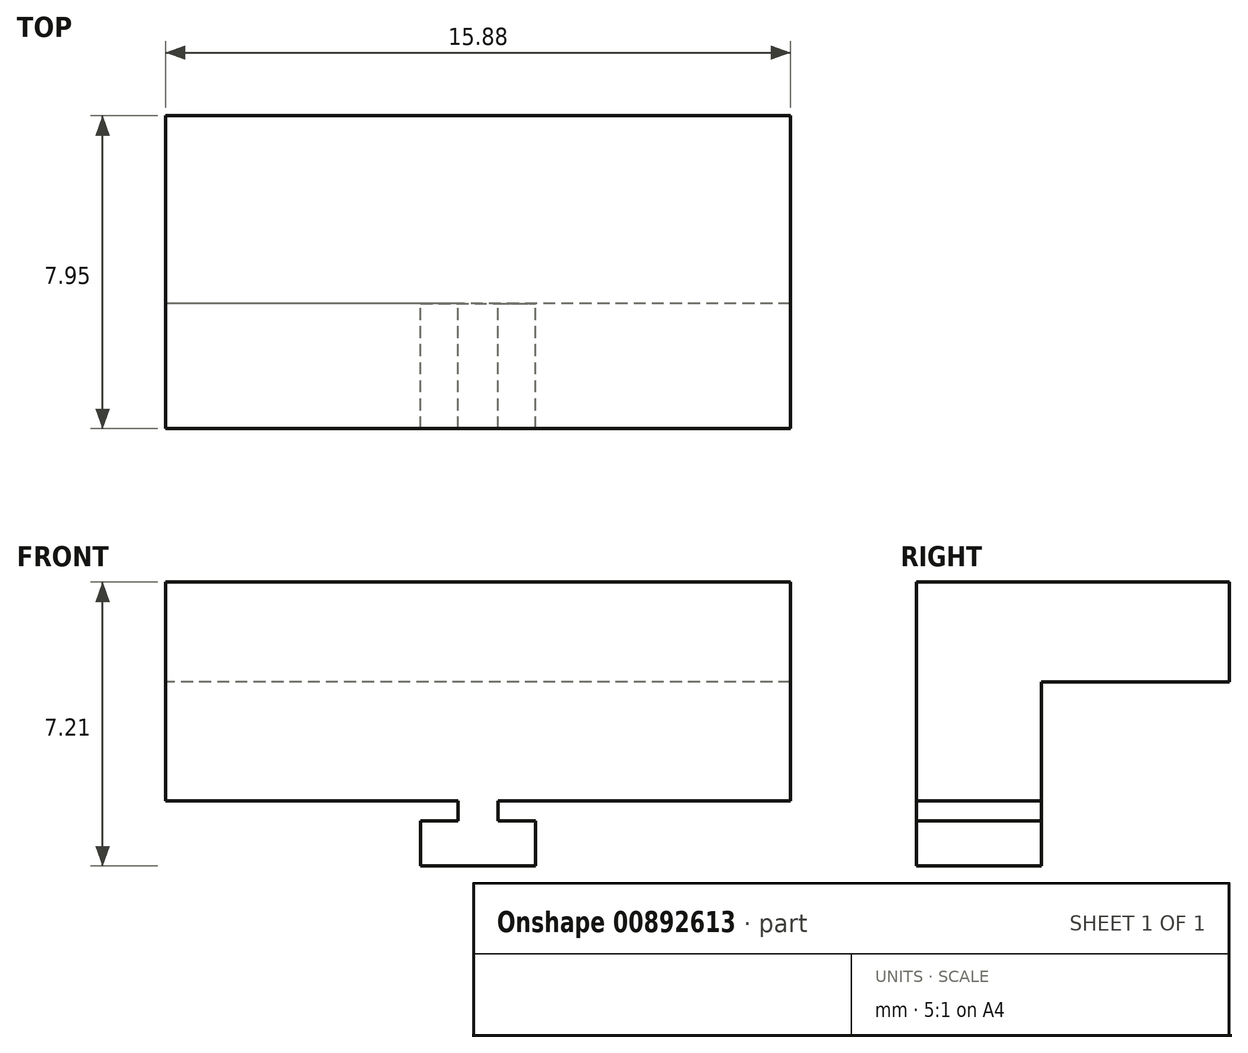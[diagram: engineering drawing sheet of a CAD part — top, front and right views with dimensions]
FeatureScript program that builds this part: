
annotation { "Feature Type Name" : "Feature", "Feature Type Description" : "" }
export const myFeature = defineFeature(function(context is Context, id is Id, definition is map)
    precondition{}
    {
        {
            var Q0;
            Q0=qCreatedBy(makeId("Top.planeOp"),FACE);
            var sketch = newSketch(context, id + "F0", { "sketchPlane" : qUnion([Q0])});
            skLineSegment(sketch, "E0.bottom", {"start": v(7.94, -1.59) * mm, "end": v(-7.94, -1.59) * mm});
            skLineSegment(sketch, "E0.top", {"start": v(7.94, 1.59) * mm, "end": v(-7.94, 1.59) * mm});
            skLineSegment(sketch, "E0.left", {"start": v(7.94, -1.59) * mm, "end": v(7.94, 1.59) * mm});
            skLineSegment(sketch, "E0.right", {"start": v(-7.94, -1.59) * mm, "end": v(-7.94, 1.59) * mm});
            skPoint(sketch, "E0.middle", {"position": v(0, 0) * mm});
            skSolve(sketch);
        }
        {
            var Q0;
            Q0=makeQuery(id+"F0.imprint","IMPRINT",FACE,{"disambiguationData":[TD([[makeQuery(id+"F0.imprint","IMPRINT",EDGE,{"derivedFrom":sQuery(id+"F0.wireOp",EDGE,"E0.bottom")}),-1.0]])]});
            extrude(context, id + "F1", {"entities" : qUnion([Q0]), "depth" : 5.56 * mm, "offsetDistance" : 25.4 * mm});
        }
        {
            var Q0;
            Q0=makeQuery(id+"F1.opExtrude","SWEPT_FACE",FACE,{"disambiguationData":[OSD([sQuery(id+"F0.wireOp",EDGE,"E0.top")])]});
            var sketch = newSketch(context, id + "F2", { "sketchPlane" : qUnion([Q0])});
            skLineSegment(sketch, "E1.bottom", {"start": v(-7.94, 5.56) * mm, "end": v(7.94, 5.56) * mm});
            skLineSegment(sketch, "E1.top", {"start": v(-7.94, 3.02) * mm, "end": v(7.94, 3.02) * mm});
            skLineSegment(sketch, "E1.left", {"start": v(-7.94, 5.56) * mm, "end": v(-7.94, 3.02) * mm});
            skLineSegment(sketch, "E1.right", {"start": v(7.94, 5.56) * mm, "end": v(7.94, 3.02) * mm});
            skSolve(sketch);
        }
        {
            var Q0;
            Q0=makeQuery(id+"F2.imprint","IMPRINT",FACE,{"disambiguationData":[TD([[makeQuery(id+"F2.imprint","IMPRINT",EDGE,{"derivedFrom":sQuery(id+"F2.wireOp",EDGE,"E1.bottom")}),-1.0]])]});
            extrude(context, id + "F3", {"entities" : qUnion([Q0]), "operationType" : NewBodyOperationType.ADD, "depth" : 4.78 * mm, "offsetDistance" : 25.4 * mm});
        }
        {
            var Q0;
            Q0=makeQuery(id+"F1.opExtrude","CAP_FACE",FACE,{"disambiguationData":[OSD([sQuery(id+"F0.wireOp",EDGE,"E0.bottom"),sQuery(id+"F0.wireOp",EDGE,"E0.top"),sQuery(id+"F0.wireOp",EDGE,"E0.left"),sQuery(id+"F0.wireOp",EDGE,"E0.right")])],"isStart":true});
            var sketch = newSketch(context, id + "F4", { "sketchPlane" : qUnion([Q0])});
            skLineSegment(sketch, "E2.bottom", {"start": v(-0.5, 1.59) * mm, "end": v(0.5, 1.59) * mm});
            skLineSegment(sketch, "E2.top", {"start": v(-0.5, -1.59) * mm, "end": v(0.5, -1.59) * mm});
            skLineSegment(sketch, "E2.left", {"start": v(-0.5, 1.59) * mm, "end": v(-0.5, -1.59) * mm});
            skLineSegment(sketch, "E2.right", {"start": v(0.5, 1.59) * mm, "end": v(0.5, -1.59) * mm});
            skPoint(sketch, "E2.middle", {"position": v(0, 0) * mm});
            skSolve(sketch);
        }
        {
            var Q0;
            Q0=makeQuery(id+"F4.imprint","IMPRINT",FACE,{"disambiguationData":[TD([[makeQuery(id+"F4.imprint","IMPRINT",EDGE,{"derivedFrom":sQuery(id+"F4.wireOp",EDGE,"E2.bottom")}),1.0]])]});
            extrude(context, id + "F5", {"entities" : qUnion([Q0]), "operationType" : NewBodyOperationType.ADD, "depth" : 0.5 * mm, "offsetDistance" : 25.4 * mm});
        }
        {
            var Q0;
            Q0=makeQuery(id+"F5.opExtrude","CAP_FACE",FACE,{"disambiguationData":[OSD([sQuery(id+"F4.wireOp",EDGE,"E2.bottom"),sQuery(id+"F4.wireOp",EDGE,"E2.top"),sQuery(id+"F4.wireOp",EDGE,"E2.left"),sQuery(id+"F4.wireOp",EDGE,"E2.right")])],"isStart":false});
            var sketch = newSketch(context, id + "F6", { "sketchPlane" : qUnion([Q0])});
            skLineSegment(sketch, "E3.bottom", {"start": v(-1.46, 1.59) * mm, "end": v(1.46, 1.59) * mm});
            skLineSegment(sketch, "E3.top", {"start": v(-1.46, -1.59) * mm, "end": v(1.46, -1.59) * mm});
            skLineSegment(sketch, "E3.left", {"start": v(-1.46, 1.59) * mm, "end": v(-1.46, -1.59) * mm});
            skLineSegment(sketch, "E3.right", {"start": v(1.46, 1.59) * mm, "end": v(1.46, -1.59) * mm});
            skPoint(sketch, "E3.middle", {"position": v(0, 0) * mm});
            skSolve(sketch);
        }
        {
            var Q0;
            {var subQ2=sQuery(id+"F6.wireOp",EDGE,"E3.right");Q0=makeQuery(id+"F6.imprint","IMPRINT",FACE,{"disambiguationData":[TD([[makeQuery(id+"F6.imprint","IMPRINT",EDGE,{"derivedFrom":subQ2}),-1.0]])]});}
            var Q1;
            {var subQ2=makeQuery(id+"F5.opExtrude","CAP_EDGE",EDGE,{"disambiguationData":[OSD([sQuery(id+"F4.wireOp",EDGE,"E2.left")])],"isStart":false});Q1=makeQuery(id+"F6.imprint","IMPRINT",FACE,{"disambiguationData":[TD([[makeQuery(id+"F6.imprint","IMPRINT",EDGE,{"derivedFrom":subQ2}),1.0]])]});}
            var Q2;
            {var subQ2=sQuery(id+"F6.wireOp",EDGE,"E3.left");Q2=makeQuery(id+"F6.imprint","IMPRINT",FACE,{"disambiguationData":[TD([[makeQuery(id+"F6.imprint","IMPRINT",EDGE,{"derivedFrom":subQ2}),1.0]])]});}
            extrude(context, id + "F7", {"entities" : qUnion([Q0, Q1, Q2]), "operationType" : NewBodyOperationType.ADD, "depth" : 1.14 * mm, "offsetDistance" : 25.4 * mm});
        }
    });
